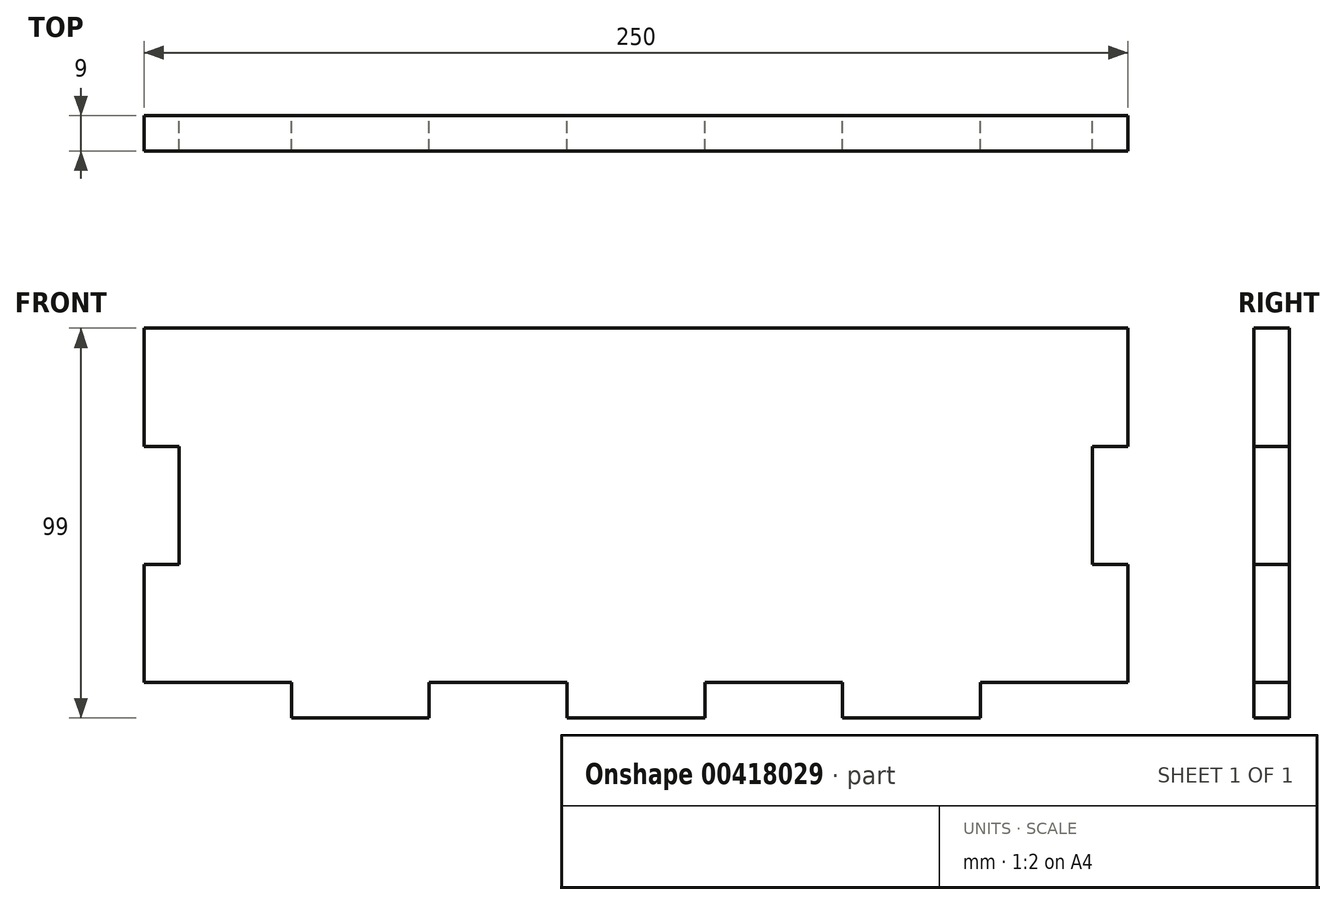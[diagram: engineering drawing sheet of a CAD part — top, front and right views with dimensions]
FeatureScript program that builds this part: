
annotation { "Feature Type Name" : "Feature", "Feature Type Description" : "" }
export const myFeature = defineFeature(function(context is Context, id is Id, definition is map)
    precondition{}
    {
        {
            var Q0;
            Q0=qCreatedBy(makeId("Front.planeOp"),FACE);
            var sketch = newSketch(context, id + "F0", { "sketchPlane" : qUnion([Q0])});
            skLineSegment(sketch, "E0", {"start": v(0, 0) * mm, "end": v(-125, 0) * mm, "construction": true});
            skLineSegment(sketch, "E1", {"start": v(-125, 0) * mm, "end": v(-125, 90) * mm, "construction": true});
            skLineSegment(sketch, "E2", {"start": v(-125, 90) * mm, "end": v(0, 90) * mm, "construction": true});
            skLineSegment(sketch, "E3", {"start": v(-125, 0) * mm, "end": v(-125, -9) * mm, "construction": true});
            skLineSegment(sketch, "E4", {"start": v(-125, -9) * mm, "end": v(0, -9) * mm, "construction": true});
            skLineSegment(sketch, "E5", {"start": v(-116, 90) * mm, "end": v(-116, 0) * mm, "construction": true});
            skLineSegment(sketch, "E6", {"start": v(-125, 90) * mm, "end": v(0, 90) * mm});
            skLineSegment(sketch, "E7", {"start": v(-125, 90) * mm, "end": v(-125, 60) * mm});
            skLineSegment(sketch, "E8", {"start": v(-125, 60) * mm, "end": v(-116, 60) * mm});
            skLineSegment(sketch, "E9", {"start": v(-116, 60) * mm, "end": v(-116, 30) * mm});
            skLineSegment(sketch, "E10", {"start": v(-116, 30) * mm, "end": v(-125, 30) * mm});
            skLineSegment(sketch, "E11", {"start": v(-125, 30) * mm, "end": v(-125, 0) * mm});
            skLineSegment(sketch, "E12", {"start": v(-116, 0) * mm, "end": v(-87.5, 0) * mm});
            skLineSegment(sketch, "E13", {"start": v(-87.5, 0) * mm, "end": v(-87.5, -9) * mm});
            skLineSegment(sketch, "E14", {"start": v(-87.5, -9) * mm, "end": v(-52.5, -9) * mm});
            skLineSegment(sketch, "E15", {"start": v(-52.5, -9) * mm, "end": v(-52.5, 0) * mm});
            skLineSegment(sketch, "E16", {"start": v(-52.5, 0) * mm, "end": v(-17.5, 0) * mm});
            skLineSegment(sketch, "E17", {"start": v(-17.5, 0) * mm, "end": v(-17.5, -9) * mm});
            skLineSegment(sketch, "E18", {"start": v(-17.5, -9) * mm, "end": v(0, -9) * mm});
            skLineSegment(sketch, "E19.MirrorCS", {"start": v(125, 90) * mm, "end": v(0, 90) * mm});
            skLineSegment(sketch, "E20.MirrorCS", {"start": v(125, 90) * mm, "end": v(125, 60) * mm});
            skLineSegment(sketch, "E21.MirrorCS", {"start": v(125, 60) * mm, "end": v(116, 60) * mm});
            skLineSegment(sketch, "E22.MirrorCS", {"start": v(116, 60) * mm, "end": v(116, 30) * mm});
            skLineSegment(sketch, "E23.MirrorCS", {"start": v(116, 30) * mm, "end": v(125, 30) * mm});
            skLineSegment(sketch, "E24.MirrorCS", {"start": v(125, 30) * mm, "end": v(125, 0) * mm});
            skLineSegment(sketch, "E25.MirrorCS", {"start": v(87.5, 0) * mm, "end": v(87.5, -9) * mm});
            skLineSegment(sketch, "E26.MirrorCS", {"start": v(87.5, -9) * mm, "end": v(52.5, -9) * mm});
            skLineSegment(sketch, "E27.MirrorCS", {"start": v(52.5, -9) * mm, "end": v(52.5, 0) * mm});
            skLineSegment(sketch, "E28.MirrorCS", {"start": v(52.5, 0) * mm, "end": v(17.5, 0) * mm});
            skLineSegment(sketch, "E29.MirrorCS", {"start": v(17.5, 0) * mm, "end": v(17.5, -9) * mm});
            skLineSegment(sketch, "E30.MirrorCS", {"start": v(17.5, -9) * mm, "end": v(0, -9) * mm});
            skLineSegment(sketch, "E31", {"start": v(-125, 0) * mm, "end": v(-87.5, 0) * mm});
            skLineSegment(sketch, "E32.MirrorCS", {"start": v(125, 0) * mm, "end": v(87.5, 0) * mm});
            skSolve(sketch);
        }
        {
            var Q0;
            Q0 = qSketchRegion(id + "F0", true);
            extrude(context, id + "F1", {"entities" : qUnion([Q0]), "depth" : 9 * mm});
        }
    });
